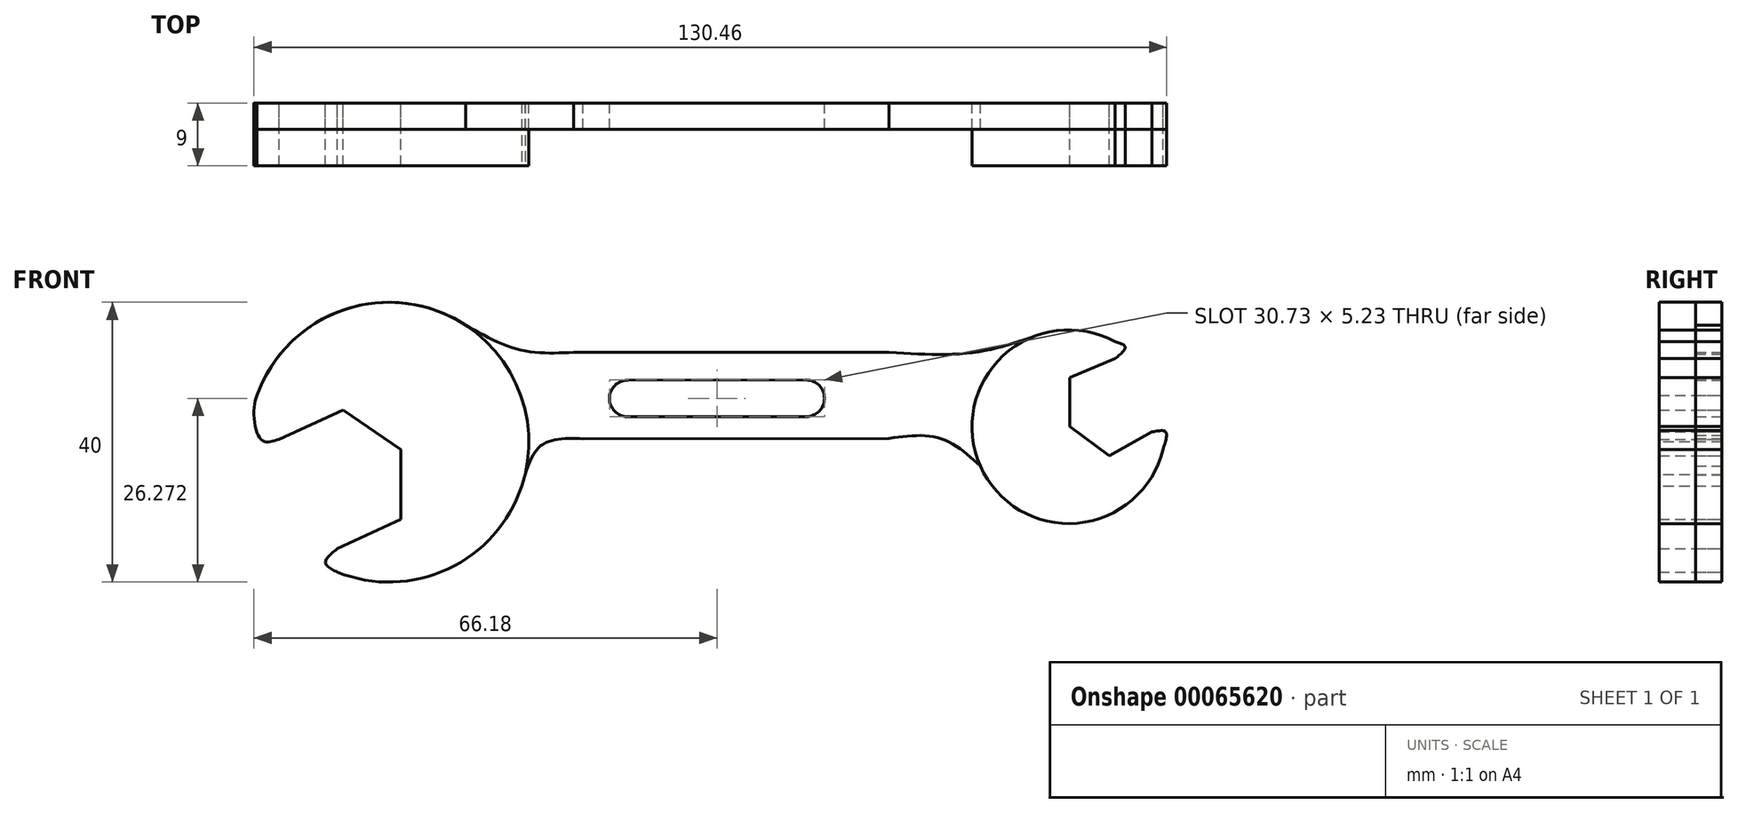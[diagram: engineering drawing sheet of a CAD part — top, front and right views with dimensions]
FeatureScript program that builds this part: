
annotation { "Feature Type Name" : "Feature", "Feature Type Description" : "" }
export const myFeature = defineFeature(function(context is Context, id is Id, definition is map)
    precondition{}
    {
        {
            var Q0;
            Q0=qCreatedBy(makeId("Front.planeOp"),FACE);
            var sketch = newSketch(context, id + "F0", { "sketchPlane" : qUnion([Q0])});
            skLineSegment(sketch, "E0", {"start": v(-32.42, 9.37) * mm, "end": v(-32.42, -0.63) * mm});
            skLineSegment(sketch, "E1", {"start": v(-32.42, 9.37) * mm, "end": v(-40.7, 14.97) * mm});
            skPoint(sketch, "E2.endSnap0", {"position": v(-36.56, 12.17) * mm});
            skLineSegment(sketch, "E3", {"start": v(-40.7, 14.97) * mm, "end": v(-49.78, 10.78) * mm});
            skLineSegment(sketch, "E4", {"start": v(-32.42, -0.63) * mm, "end": v(-41.5, -4.82) * mm});
            skFitSpline(sketch, "E5", {"points": [v(-41.5, -4.82) * mm, v(-43.18, -6.84) * mm, v(-41.5, -8.2) * mm], "startDerivative": vector(-4.98, -4.13) * mm, "endDerivative": vector(5.15, -2.6) * mm});
            skFitSpline(sketch, "E6", {"points": [v(-49.78, 10.78) * mm, v(-52.44, 10.78) * mm, v(-52.97, 17.08) * mm], "startDerivative": vector(-7.32, -1.38) * mm, "endDerivative": vector(3.78, 7.26) * mm});
            skArc(sketch, "E7", {"start": v(-41.5, -8.2) * mm, "mid": v(-15.9, 18.66) * mm, "end": v(-52.97, 17.08) * mm});
            skFitSpline(sketch, "E8", {"points": [v(-23.17, 27.13) * mm, v(-15.42, 23.62) * mm, v(-7.71, 23.23) * mm], "startDerivative": vector(14.97, -8.39) * mm, "endDerivative": vector(15.97, 0.68) * mm});
            skFitSpline(sketch, "E9", {"points": [v(-15.15, 4.06) * mm, v(-12.34, 9.93) * mm, v(-6.36, 10.9) * mm], "startDerivative": vector(3.87, 13.95) * mm, "endDerivative": vector(13.8, -0.38) * mm});
            skLineSegment(sketch, "E10", {"start": v(-7.71, 23.23) * mm, "end": v(37.4, 23.23) * mm});
            skLineSegment(sketch, "E11", {"start": v(-6.36, 10.9) * mm, "end": v(37.4, 10.95) * mm});
            skLineSegment(sketch, "E12", {"start": v(63.23, 19.63) * mm, "end": v(63.23, 12.63) * mm});
            skLineSegment(sketch, "E13", {"start": v(63.23, 12.63) * mm, "end": v(68.85, 8.45) * mm});
            skLineSegment(sketch, "E14", {"start": v(68.85, 8.45) * mm, "end": v(74.97, 11.85) * mm});
            skLineSegment(sketch, "E15", {"start": v(63.23, 19.63) * mm, "end": v(69.68, 22.34) * mm});
            skFitSpline(sketch, "E16", {"points": [v(69.68, 22.34) * mm, v(71.14, 24) * mm, v(69.68, 24.77) * mm], "startDerivative": vector(4.27, 3.47) * mm, "endDerivative": vector(-4.49, 1.33) * mm});
            skFitSpline(sketch, "E17", {"points": [v(74.97, 11.85) * mm, v(76.92, 11.85) * mm, v(76.53, 9.35) * mm], "startDerivative": vector(5.31, 1.1) * mm, "endDerivative": vector(-2.03, -5.95) * mm});
            skArc(sketch, "E18", {"start": v(69.68, 24.77) * mm, "mid": v(50.43, 6.99) * mm, "end": v(76.53, 9.35) * mm});
            skFitSpline(sketch, "E19", {"points": [v(37.4, 23.23) * mm, v(49.54, 23.23) * mm, v(58.44, 25.65) * mm], "startDerivative": vector(23.7, -1.38) * mm, "endDerivative": vector(18.27, 6.37) * mm});
            skLineSegment(sketch, "E20", {"start": v(0, 19.25) * mm, "end": v(25.52, 19.29) * mm});
            skLineSegment(sketch, "E21", {"start": v(0, 14.06) * mm, "end": v(25.52, 14.06) * mm});
            skArc(sketch, "E22", {"start": v(0, 19.25) * mm, "mid": v(-2.6, 16.65) * mm, "end": v(0, 14.06) * mm});
            skArc(sketch, "E23", {"start": v(25.52, 14.06) * mm, "mid": v(28.14, 16.67) * mm, "end": v(25.52, 19.29) * mm});
            skFitSpline(sketch, "E24", {"points": [v(37.4, 10.95) * mm, v(44.63, 10.95) * mm, v(50.43, 6.99) * mm], "startDerivative": vector(15.03, 2.01) * mm, "endDerivative": vector(11.01, -9.98) * mm});
            skSolve(sketch);
        }
        {
            var Q0;
            Q0=makeQuery(id+"F0.imprint","IMPRINT",FACE,{"disambiguationData":[TD([[makeQuery(id+"F0.imprint","IMPRINT",EDGE,{"derivedFrom":sQuery(id+"F0.wireOp",EDGE,"E0")}),1.0]])]});
            var Q1;
            Q1=makeQuery(id+"F0.imprint","IMPRINT",FACE,{"disambiguationData":[TD([[makeQuery(id+"F0.imprint","IMPRINT",EDGE,{"derivedFrom":sQuery(id+"F0.wireOp",EDGE,"E12")}),-1.0]])]});
            extrude(context, id + "F1", {"entities" : qUnion([Q0, Q1]), "depth" : 9 * mm});
        }
        {
            var Q0;
            Q0 = qSketchRegion(id + "F0", true);
            extrude(context, id + "F2", {"entities" : qUnion([Q0]), "depth" : 3.76 * mm});
        }
    });
